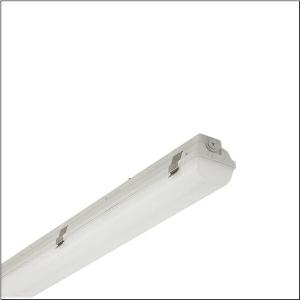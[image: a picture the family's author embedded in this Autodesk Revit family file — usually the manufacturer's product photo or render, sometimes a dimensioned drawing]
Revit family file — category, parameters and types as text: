
# Revit family: monsun_r__21_eco_51fj20ml45a_05e8
name_source: partatom
category: Lighting Fixtures
units: mm (PartAtom-declared; Revit-internal decimal feet)

## family parameters
Cut with Voids When Loaded = No
Host = Face
Light Source = No
Part Type = Normal
Room Calculation Point = No
Round Connector Dimension = Use Diameter
Shared = No

## types (1)
- --- (1 x LED, 4900 lm, 36 W, 4000K)
    Apparent Load = 36 VA
    CIE Flux Codes = 40 69 88 88 100
    Color Rendering = 80
    Color Temperature = 4000K
    Default Elevation = 1800 mm
    Description = Monsun® 21 Eco, damp-proof luminaire, primary optical cover: diffuser, of PC, UV-stabilised, frosted, light emission: direct distribution, primary light characteristic: symmetric, installation type: suspended mounting, surface-mounted, LED, rated luminous flux: 4.900lm, luminous efficacy: 132lm/W, light colour: 840, colour temperature: 4000K, control gear: ON/OFF Multilumen, with terminal, 3-pole, max. 2.5mm², mains connection: 220..240V, AC, 50/60Hz, rated input power: 36W, housing, of glass-fibre reinforced polyester, light grey (RAL 7035), length: 1.277mm, width: 90mm, height: 95mm, clip for enclosure, of spring steel V2A, protection rating (complete): IP66, insulation class (complete): insulation class I (protective earthing), certification: CE, UKCA, protection symbol: D, impact resistance: IK08, permissible operating ambient temperature: -20..+35°C, corresponds to IFS (International Featured Standards) requirements for safety and quality in the food industry, contact your sales advisor before using the luminaires in applications with unclear chemical exposure, large temperature fluctuations or condensation-forming humidity, packaging unit: 1 piece
    Height = 103 mm
    Lamp = 1 x LED
    Lamp Light Flux = 4900 lm
    Lamp Power = 36 W
    Lamp count = 1
    Length = 1277 mm
    Luminous efficacy = 136 lm/W
    Manufacturer = Siteco
    ModVariant = No
    Model = 51FJ20ML45A
    Mounting Place = Ceiling
    Mounting Type = Surface mounted
    Number of Poles = 1
    OnlyDefault = Yes
    Power Factor = 1
    Product Name = Monsun® 21 Eco
    Product group = damp-proof luminaire
    ProductGroupID = 300
    Protection Class = Protection class I
    Protection Degree = IP 66
    RLX_Detail_Level = 1
    RLX_Emergency_Light_Flux = 0 lm
    RLX_Emergency_Type = 0
    RLX_Emergency_Type_DB = No
    RlxData = <blob elided: 34097 chars, md5=42d7563f>
    Socket = socket
    Standby Power = 0 W
    System Light Flux = 4900 lm
    System Power = 36 W
    Type Comments = factory setting: luminous flux: 100 % | (ON | ON) | 350 mA
    Type Image = l_1007218.jpg
    URL = http://relux.com
    VarID = @adj_146186
    Voltage = 0 V
    Weight = 0.00 kg
    Width = 90 mm

## geometry (parser evidence)
native form markers: Blend x4, Sweep x12
no freeform markers — native parametric forms only
